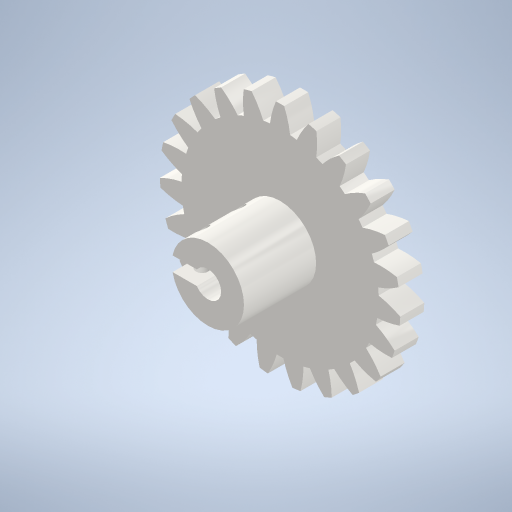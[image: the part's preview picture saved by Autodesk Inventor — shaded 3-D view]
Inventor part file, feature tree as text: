
AUTODESK INVENTOR PART (.ipt)
format: ipt  version: 2023 (Build 270158000, 158)  size: 569,856 bytes
history: native  units: mm (DEFAULTED — no unit token found)
features: extrude x4, sketch x4, projected_geometry x4, plane x3, other x3
ambient origin geometry x8: Origin, YZ Plane, XZ Plane, XY Plane, X Axis, Y Axis, Z Axis, Center Point
bodies: Solid1 (feature_tree)
feature tree (18):
  extrude  "Extrusion1"  Depth=5.0mm TaperAngle=0.0deg
  plane  "Work Plane2"
  plane  "Work Plane8"
  plane  "Work Plane9"
  other  "Spur Gear"
  extrude  "Extrusion2"  Depth=10.0mm TaperAngle=0.0deg
  extrude  "Extrusion3"  Depth=1.36591mm TaperAngle=0.0deg
  extrude  "Extrusion4"  TaperAngle=0.0deg  [1 undecoded]
  sketch  "Sketch1"  dims[d0=50.0mm d1=5.0mm d2=0.0mm]
  sketch  "Sketch2"  dims[d3=46.0mm d4=10.0mm d5=0.0mm]
  other  "Srf1"
  sketch  "Sketch3"  dims[d16=80.0mm d17=0.0mm d34=1.36591mm]
  projected_geometry  "Projected Loop1"
  sketch  "Sketch5"  dims[d39=0.0mm d41=0.0mm d43=80.0mm d46=80.0mm d47=0.0mm d48=0.0mm d49=5.5mm d50=5.0mm d51=0.0mm d52=15.0mm d53=3.0mm d54=15.0mm d55=0.0mm d56=2.0mm d57=15.0mm d58=0.0mm d59=15.0mm d60=2.5mm d61=2.5mm]
  projected_geometry  "Projected Loop3"
  projected_geometry  "Projected Loop4"
  projected_geometry  "Projected Loop5"
  other  "Pitch Diameter"
note: 1 required parameter value undecoded (feature->parameter linkage not recoverable at this tier; creation-order binding heuristic only, values carry confidence <= 0.55)
